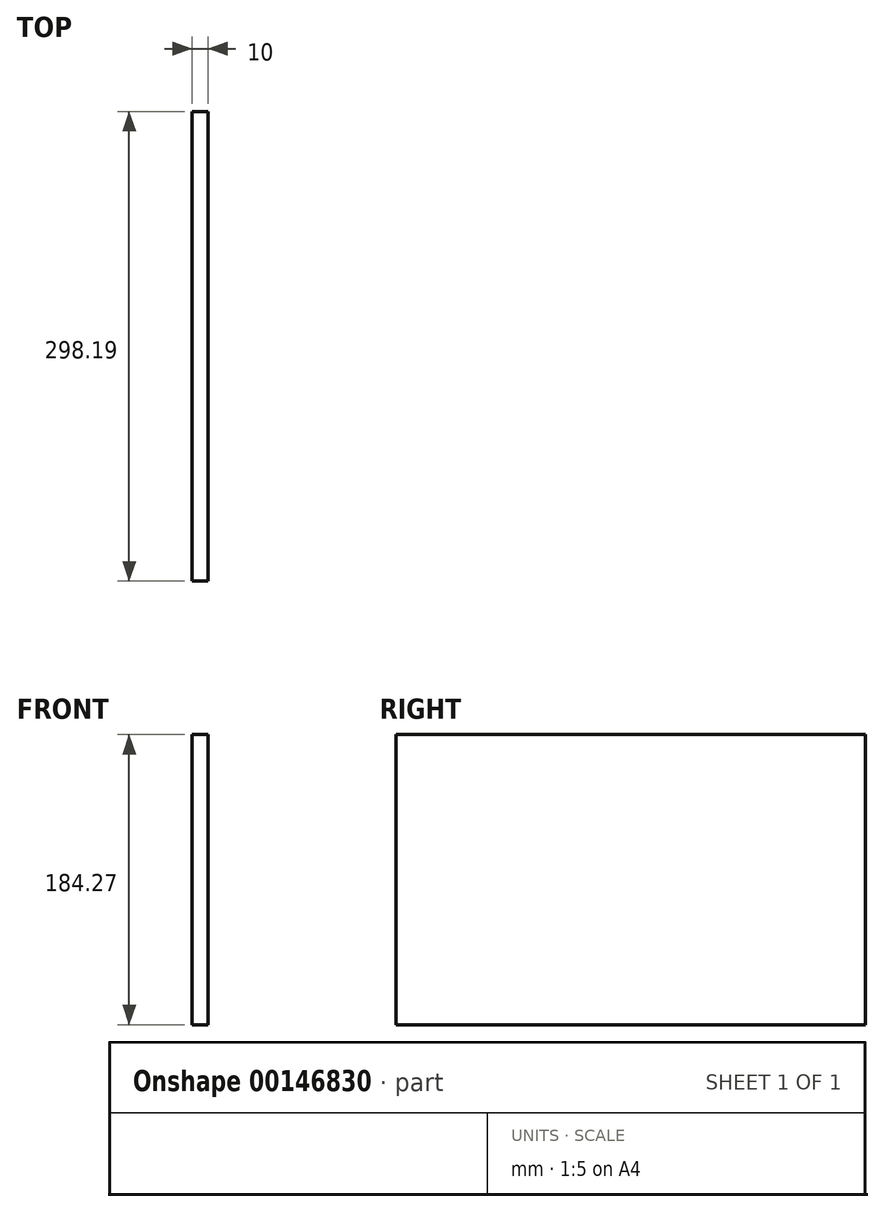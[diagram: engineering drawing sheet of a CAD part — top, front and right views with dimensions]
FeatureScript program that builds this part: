
annotation { "Feature Type Name" : "Feature", "Feature Type Description" : "" }
export const myFeature = defineFeature(function(context is Context, id is Id, definition is map)
    precondition{}
    {
        {
            var Q0;
            Q0=qCreatedBy(makeId("Right.planeOp"),FACE);
            var sketch = newSketch(context, id + "F0", { "sketchPlane" : qUnion([Q0])});
            skLineSegment(sketch, "E0.bottom", {"start": v(0, 0) * mm, "end": v(-298.19, 0) * mm});
            skLineSegment(sketch, "E0.top", {"start": v(0, 184.27) * mm, "end": v(-298.19, 184.27) * mm});
            skLineSegment(sketch, "E0.left", {"start": v(0, 0) * mm, "end": v(0, 184.27) * mm});
            skLineSegment(sketch, "E0.right", {"start": v(-298.19, 0) * mm, "end": v(-298.19, 184.27) * mm});
            skSolve(sketch);
        }
        {
            var Q0;
            Q0=makeQuery(id+"F0.imprint","IMPRINT",FACE,{"disambiguationData":[TD([[makeQuery(id+"F0.imprint","IMPRINT",EDGE,{"derivedFrom":sQuery(id+"F0.wireOp",EDGE,"E0.bottom")}),-1.0]])]});
            extrude(context, id + "F1", {"entities" : qUnion([Q0]), "depth" : 10 * mm});
        }
    });
